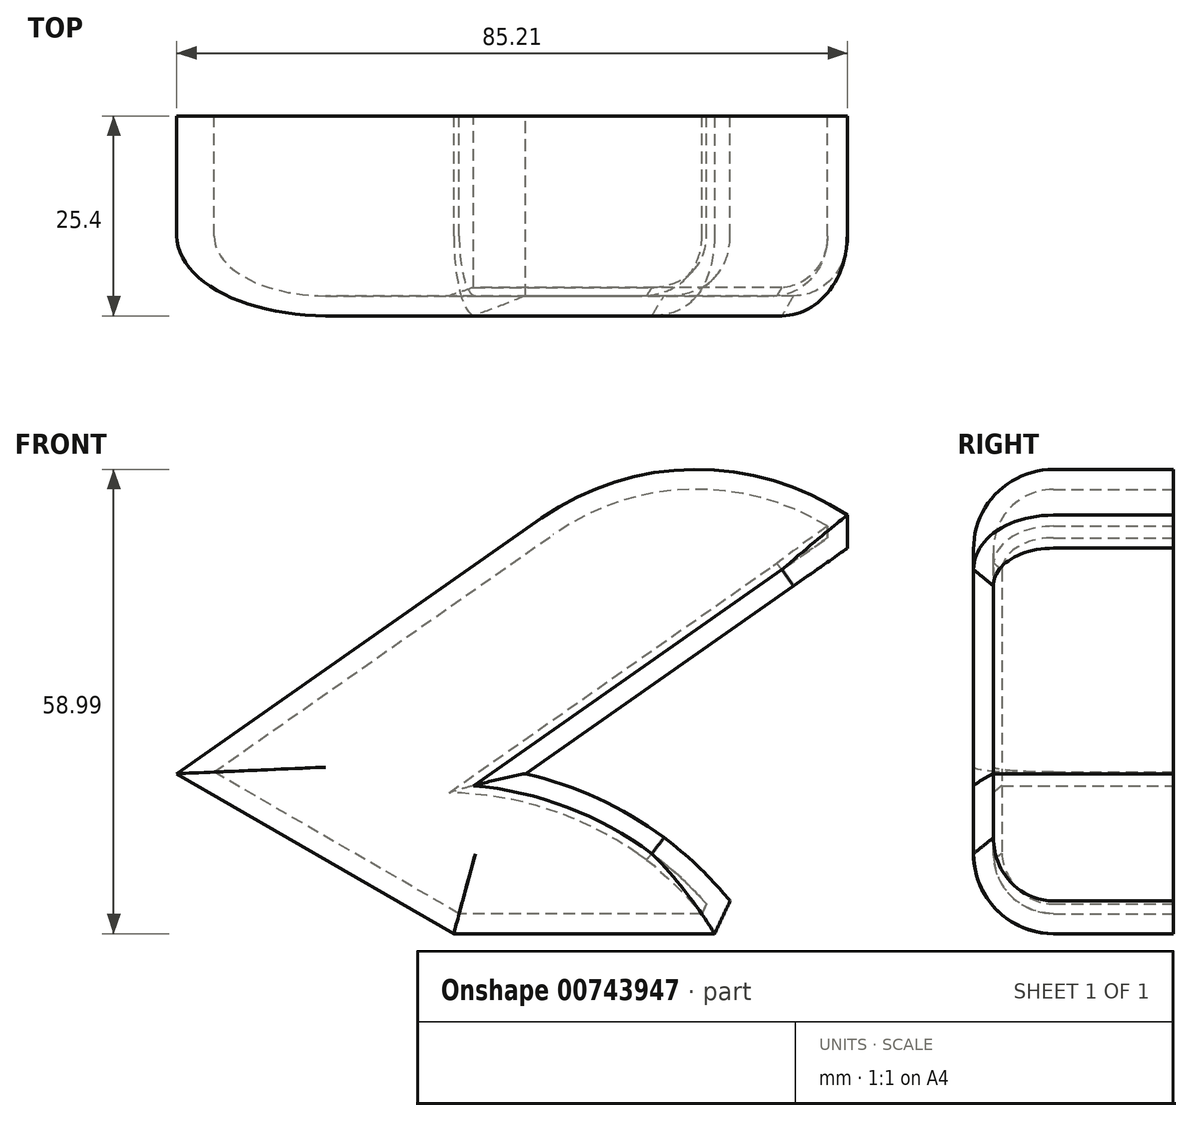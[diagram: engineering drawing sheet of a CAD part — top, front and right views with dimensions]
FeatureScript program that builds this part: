
annotation { "Feature Type Name" : "Feature", "Feature Type Description" : "" }
export const myFeature = defineFeature(function(context is Context, id is Id, definition is map)
    precondition{}
    {
        {
            var Q0;
            Q0=qCreatedBy(makeId("Front.planeOp"),FACE);
            var sketch = newSketch(context, id + "F0", { "sketchPlane" : qUnion([Q0])});
            skLineSegment(sketch, "E0", {"start": v(0, 0) * mm, "end": v(-38.1, 0) * mm});
            skLineSegment(sketch, "E1", {"start": v(-38.1, 0) * mm, "end": v(-73.3, 20.32) * mm});
            skLineSegment(sketch, "E2", {"start": v(-73.3, 20.32) * mm, "end": v(0, 71.64) * mm});
            skLineSegment(sketch, "E3", {"start": v(-29.01, 20.32) * mm, "end": v(44.28, 71.64) * mm});
            skLineSegment(sketch, "E4", {"start": v(-73.3, 20.32) * mm, "end": v(43.2, 20.32) * mm, "construction": true});
            skLineSegment(sketch, "E5", {"start": v(0, 71.64) * mm, "end": v(88.57, 71.64) * mm, "construction": true});
            skArc(sketch, "E6", {"start": v(0, 0) * mm, "mid": v(-12.52, 13) * mm, "end": v(-29.01, 20.32) * mm});
            skArc(sketch, "E7", {"start": v(14.77, 50.98) * mm, "mid": v(-5.78, 58.95) * mm, "end": v(-26.94, 52.78) * mm});
            skSolve(sketch);
        }
        {
            var Q0;
            Q0=makeQuery(id+"F0.imprint","IMPRINT",FACE,{"disambiguationData":[TD([[makeQuery(id+"F0.imprint","IMPRINT",EDGE,{"derivedFrom":sQuery(id+"F0.wireOp",EDGE,"E0")}),-1.0]])]});
            extrude(context, id + "F1", {"entities" : qUnion([Q0]), "depth" : 25.4 * mm, "offsetDistance" : 25.4 * mm});
        }
        {
            var Q0;
            Q0=makeQuery(id+"F1.opExtrude","CAP_EDGE",EDGE,{"disambiguationData":[OSD([sQuery(id+"F0.wireOp",EDGE,"E2")])],"isStart":false});
            var Q1;
            Q1=makeQuery(id+"F1.opExtrude","CAP_EDGE",EDGE,{"disambiguationData":[OSD([sQuery(id+"F0.wireOp",EDGE,"E1")])],"isStart":false});
            var Q2;
            Q2=makeQuery(id+"F1.opExtrude","CAP_EDGE",EDGE,{"disambiguationData":[OSD([sQuery(id+"F0.wireOp",EDGE,"E0")])],"isStart":false});
            fillet(context, id + "F2", {"entities" : qUnion([Q0, Q1, Q2]), "radius" : 10.16 * mm, "tangentPropagation" : true, "allowEdgeOverflow" : false});
        }
        {
            var Q0;
            Q0=makeQuery(id+"F2.opFillet","BLEND_EDGE",EDGE,{"blendedFrom":[makeQuery(id+"F1.opExtrude","CAP_EDGE",EDGE,{"disambiguationData":[OSD([sQuery(id+"F0.wireOp",EDGE,"E7")])],"isStart":false}),makeQuery(id+"F1.opExtrude","SWEPT_FACE",FACE,{"disambiguationData":[OSD([sQuery(id+"F0.wireOp",EDGE,"E3")])]})],"blendedInto":[makeQuery(id+"F1.opExtrude","SWEPT_FACE",FACE,{"disambiguationData":[OSD([sQuery(id+"F0.wireOp",EDGE,"E3")])]})]});
            var Q1;
            Q1=makeQuery(id+"F2.opFillet","BLEND_EDGE",EDGE,{"blendedFrom":[makeQuery(id+"F1.opExtrude","CAP_EDGE",EDGE,{"disambiguationData":[OSD([sQuery(id+"F0.wireOp",EDGE,"E0")])],"isStart":false}),makeQuery(id+"F1.opExtrude","SWEPT_FACE",FACE,{"disambiguationData":[OSD([sQuery(id+"F0.wireOp",EDGE,"E6")])]})],"blendedInto":[makeQuery(id+"F1.opExtrude","SWEPT_FACE",FACE,{"disambiguationData":[OSD([sQuery(id+"F0.wireOp",EDGE,"E6")])]})]});
            chamfer(context, id + "F3", {"entities" : qUnion([Q0, Q1]), "width" : 2.54 * mm, "tangentPropagation" : true});
        }
        {
            var Q0;
            Q0=makeQuery(id+"F1.opExtrude","CAP_FACE",FACE,{"disambiguationData":[OSD([sQuery(id+"F0.wireOp",EDGE,"E0"),sQuery(id+"F0.wireOp",EDGE,"E1"),sQuery(id+"F0.wireOp",EDGE,"E2"),sQuery(id+"F0.wireOp",EDGE,"E3"),sQuery(id+"F0.wireOp",EDGE,"E6"),sQuery(id+"F0.wireOp",EDGE,"E7")])],"isStart":true});
            shell(context, id + "F4", {"entities" : qUnion([Q0]), "thickness" : 2.54 * mm});
        }
    });
